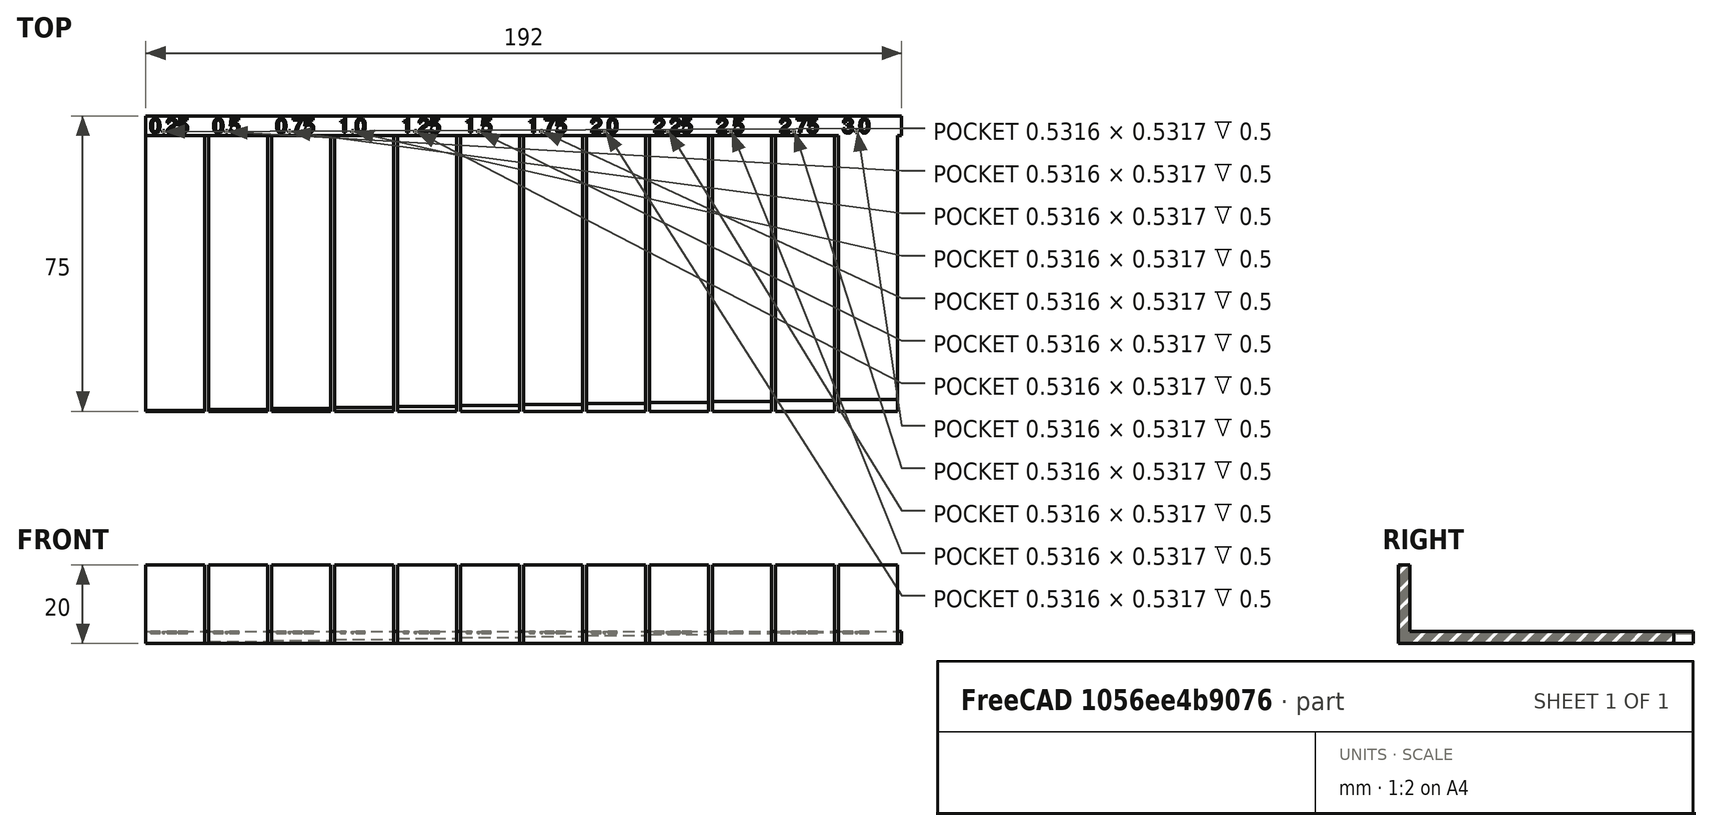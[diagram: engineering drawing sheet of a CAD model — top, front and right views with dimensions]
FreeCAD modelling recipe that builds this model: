
FCSTD DOCUMENT  (FreeCAD 0.18R16093 (Git))
Label: thickness test
License: All rights reserved
LicenseURL: http://en.wikipedia.org/wiki/All_rights_reserved
objects: Part::Box×25, Part::Part2DObjectPython×12, Part::Extrusion×12, Part::MultiFuse×4, App::DocumentObjectGroup×3, Part::Cut×1
note: 54 computed .brp shape members not serialized (recipe doc carries the construction recipe); baked Part::Feature solids carry a one-line shape summary decoded from their .brp

FEATURE [Part::Box] Box  label="Cube000"
  AttacherType = Attacher::AttachEngine3D
  Height = 0.25
  Length = 15
  Width = 70
FEATURE [Part::Box] Box001  label="Cube001"
  AttacherType = Attacher::AttachEngine3D
  Height = 0.5
  Length = 15
  Placement = pos=(16,0,0) rot=(0,0,1;0rad)
  Width = 70
FEATURE [Part::Box] Box002  label="Cube002"
  AttacherType = Attacher::AttachEngine3D
  Height = 0.75
  Length = 15
  Placement = pos=(32,0,0) rot=(0,0,1;0rad)
  Width = 70
FEATURE [Part::Box] Box003  label="Cube003"
  AttacherType = Attacher::AttachEngine3D
  Height = 1
  Length = 15
  Placement = pos=(48,0,0) rot=(0,0,1;0rad)
  Width = 70
FEATURE [Part::Box] Box004  label="Cube004"
  AttacherType = Attacher::AttachEngine3D
  Height = 1.25
  Length = 15
  Placement = pos=(64,0,0) rot=(0,0,1;0rad)
  Width = 70
FEATURE [Part::Box] Box005  label="Cube005"
  AttacherType = Attacher::AttachEngine3D
  Height = 1.5
  Length = 15
  Placement = pos=(80,0,0) rot=(0,0,1;0rad)
  Width = 70
FEATURE [Part::Box] Box006  label="Cube006"
  AttacherType = Attacher::AttachEngine3D
  Height = 1.75
  Length = 15
  Placement = pos=(96,0,0) rot=(0,0,1;0rad)
  Width = 70
FEATURE [Part::Box] Box007  label="Cube007"
  AttacherType = Attacher::AttachEngine3D
  Height = 2
  Length = 15
  Placement = pos=(112,0,0) rot=(0,0,1;0rad)
  Width = 70
FEATURE [Part::Box] Box008  label="Cube008"
  AttacherType = Attacher::AttachEngine3D
  Height = 2.25
  Length = 15
  Placement = pos=(128,0,0) rot=(0,0,1;0rad)
  Width = 70
FEATURE [Part::Box] Box009  label="Cube009"
  AttacherType = Attacher::AttachEngine3D
  Height = 2.5
  Length = 15
  Placement = pos=(144,0,0) rot=(0,0,1;0rad)
  Width = 70
FEATURE [Part::Box] Box010  label="Cube010"
  AttacherType = Attacher::AttachEngine3D
  Height = 2.75
  Length = 15
  Placement = pos=(160,0,0) rot=(0,0,1;0rad)
  Width = 70
FEATURE [Part::Box] Box011  label="Cube011"
  AttacherType = Attacher::AttachEngine3D
  Height = 3
  Length = 15
  Placement = pos=(176,0,0) rot=(0,0,1;0rad)
  Width = 70
FEATURE [Part::Box] Box012  label="Cube"
  AttacherType = Attacher::AttachEngine3D
  Height = 20
  Length = 15
  Width = 0.25
FEATURE [Part::Box] Box013  label="Cube012"
  AttacherType = Attacher::AttachEngine3D
  Height = 20
  Length = 15
  Placement = pos=(16,0,0) rot=(0,0,1;0rad)
  Width = 0.5
FEATURE [Part::Box] Box014  label="Cube013"
  AttacherType = Attacher::AttachEngine3D
  Height = 20
  Length = 15
  Placement = pos=(32,0,0) rot=(0,0,1;0rad)
  Width = 0.75
FEATURE [Part::Box] Box015  label="Cube014"
  AttacherType = Attacher::AttachEngine3D
  Height = 20
  Length = 15
  Placement = pos=(48,0,0) rot=(0,0,1;0rad)
  Width = 1
FEATURE [Part::Box] Box016  label="Cube015"
  AttacherType = Attacher::AttachEngine3D
  Height = 20
  Length = 15
  Placement = pos=(64,0,0) rot=(0,0,1;0rad)
  Width = 1.25
FEATURE [Part::Box] Box017  label="Cube016"
  AttacherType = Attacher::AttachEngine3D
  Height = 20
  Length = 15
  Placement = pos=(80,0,0) rot=(0,0,1;0rad)
  Width = 1.5
FEATURE [Part::Box] Box018  label="Cube017"
  AttacherType = Attacher::AttachEngine3D
  Height = 20
  Length = 15
  Placement = pos=(96,0,0) rot=(0,0,1;0rad)
  Width = 1.75
FEATURE [Part::Box] Box019  label="Cube018"
  AttacherType = Attacher::AttachEngine3D
  Height = 20
  Length = 15
  Placement = pos=(112,0,0) rot=(0,0,1;0rad)
  Width = 2
FEATURE [Part::Box] Box020  label="Cube019"
  AttacherType = Attacher::AttachEngine3D
  Height = 20
  Length = 15
  Placement = pos=(128,0,0) rot=(0,0,1;0rad)
  Width = 2.25
FEATURE [Part::Box] Box021  label="Cube020"
  AttacherType = Attacher::AttachEngine3D
  Height = 20
  Length = 15
  Placement = pos=(144,0,0) rot=(0,0,1;0rad)
  Width = 2.5
FEATURE [Part::Box] Box022  label="Cube021"
  AttacherType = Attacher::AttachEngine3D
  Height = 20
  Length = 15
  Placement = pos=(160,0,0) rot=(0,0,1;0rad)
  Width = 2.75
FEATURE [Part::Box] Box023  label="Cube022"
  AttacherType = Attacher::AttachEngine3D
  Height = 20
  Length = 15
  Placement = pos=(176,0,0) rot=(0,0,1;0rad)
  Width = 3
FEATURE [App::DocumentObjectGroup] Group001
FEATURE [Part::Box] Box024  label="Cube023"
  AttacherType = Attacher::AttachEngine3D
  Height = 3
  Length = 192
  Placement = pos=(0,70,0) rot=(0,0,1;0rad)
  Width = 5
FEATURE [Part::Part2DObjectPython] ShapeString001  # Draft 2D object (typed FeaturePython)
  FontFile = <path>
  Placement = pos=(17,70.75,3) rot=(0,0,1;0rad)
  Size = 2
  String = 0.5
  Tracking = 0
FEATURE [Part::Part2DObjectPython] ShapeString002  # Draft 2D object (typed FeaturePython)
  FontFile = <path>
  Placement = pos=(33,70.75,3) rot=(0,0,1;0rad)
  Size = 2
  String = 0.75
  Tracking = 0
FEATURE [Part::Part2DObjectPython] ShapeString003  # Draft 2D object (typed FeaturePython)
  FontFile = <path>
  Placement = pos=(49,70.75,3) rot=(0,0,1;0rad)
  Size = 2
  String = 1
  Tracking = 0
FEATURE [Part::Part2DObjectPython] ShapeString004  # Draft 2D object (typed FeaturePython)
  FontFile = <path>
  Placement = pos=(65,70.75,3) rot=(0,0,1;0rad)
  Size = 2
  String = 1.25
  Tracking = 0
FEATURE [Part::Part2DObjectPython] ShapeString005  # Draft 2D object (typed FeaturePython)
  FontFile = <path>
  Placement = pos=(81,70.75,3) rot=(0,0,1;0rad)
  Size = 2
  String = 1.5
  Tracking = 0
FEATURE [Part::Part2DObjectPython] ShapeString006  # Draft 2D object (typed FeaturePython)
  FontFile = <path>
  Placement = pos=(97,70.75,3) rot=(0,0,1;0rad)
  Size = 2
  String = 1.75
  Tracking = 0
FEATURE [Part::Part2DObjectPython] ShapeString007  # Draft 2D object (typed FeaturePython)
  FontFile = <path>
  Placement = pos=(113,70.75,3) rot=(0,0,1;0rad)
  Size = 2
  String = 2
  Tracking = 0
FEATURE [Part::Part2DObjectPython] ShapeString008  # Draft 2D object (typed FeaturePython)
  FontFile = <path>
  Placement = pos=(129,70.75,3) rot=(0,0,1;0rad)
  Size = 2
  String = 2.25
  Tracking = 0
  expr: Placement.Base.x = 113 + 16
FEATURE [Part::Part2DObjectPython] ShapeString009  # Draft 2D object (typed FeaturePython)
  FontFile = <path>
  Placement = pos=(145,70.75,3) rot=(0,0,1;0rad)
  Size = 2
  String = 2.5
  Tracking = 0
FEATURE [Part::Part2DObjectPython] ShapeString010  # Draft 2D object (typed FeaturePython)
  FontFile = <path>
  Placement = pos=(161,70.75,3) rot=(0,0,1;0rad)
  Size = 2
  String = 2.75
  Tracking = 0
FEATURE [Part::Part2DObjectPython] ShapeString011  # Draft 2D object (typed FeaturePython)
  FontFile = <path>
  Placement = pos=(177,70.75,3) rot=(0,0,1;0rad)
  Size = 2
  String = 3
  Tracking = 0
FEATURE [Part::Part2DObjectPython] ShapeString012  # Draft 2D object (typed FeaturePython)
  FontFile = <path>
  Placement = pos=(1,70.75,3) rot=(0,0,1;0rad)
  Size = 2
  String = 0.25
  Tracking = 0
FEATURE [App::DocumentObjectGroup] Group002
  Group = -> [ShapeString001,ShapeString002,ShapeString003,ShapeString004,ShapeString005,ShapeString006,ShapeString007,ShapeString008,ShapeString009,ShapeString010,ShapeString011,ShapeString012]
FEATURE [Part::Extrusion] Extrude
  Base = -> ShapeString001
  Dir = (0,0,1)
  DirMode = 2
  FaceMakerClass = Part::FaceMakerBullseye
  LengthFwd = 0
  LengthRev = 0.5
  Solid = false
  Symmetric = false
FEATURE [Part::Extrusion] Extrude001
  Base = -> ShapeString002
  Dir = (0,0,1)
  DirMode = 2
  FaceMakerClass = Part::FaceMakerBullseye
  LengthFwd = 0
  LengthRev = 0.5
  Solid = false
  Symmetric = false
FEATURE [Part::Extrusion] Extrude002
  Base = -> ShapeString003
  Dir = (0,0,1)
  DirMode = 2
  FaceMakerClass = Part::FaceMakerBullseye
  LengthFwd = 0
  LengthRev = 0.5
  Solid = false
  Symmetric = false
FEATURE [Part::Extrusion] Extrude003
  Base = -> ShapeString004
  Dir = (0,0,1)
  DirMode = 2
  FaceMakerClass = Part::FaceMakerBullseye
  LengthFwd = 0
  LengthRev = 0.5
  Solid = false
  Symmetric = false
FEATURE [Part::Extrusion] Extrude004
  Base = -> ShapeString005
  Dir = (0,0,1)
  DirMode = 2
  FaceMakerClass = Part::FaceMakerBullseye
  LengthFwd = 0
  LengthRev = 0.5
  Solid = false
  Symmetric = false
FEATURE [Part::Extrusion] Extrude005
  Base = -> ShapeString006
  Dir = (0,0,1)
  DirMode = 2
  FaceMakerClass = Part::FaceMakerBullseye
  LengthFwd = 0
  LengthRev = 0.5
  Solid = false
  Symmetric = false
FEATURE [Part::Extrusion] Extrude006
  Base = -> ShapeString007
  Dir = (0,0,1)
  DirMode = 2
  FaceMakerClass = Part::FaceMakerBullseye
  LengthFwd = 0
  LengthRev = 0.5
  Solid = false
  Symmetric = false
FEATURE [Part::Extrusion] Extrude007
  Base = -> ShapeString008
  Dir = (0,0,1)
  DirMode = 2
  FaceMakerClass = Part::FaceMakerBullseye
  LengthFwd = 0
  LengthRev = 0.5
  Solid = false
  Symmetric = false
FEATURE [Part::Extrusion] Extrude008
  Base = -> ShapeString009
  Dir = (0,0,1)
  DirMode = 2
  FaceMakerClass = Part::FaceMakerBullseye
  LengthFwd = 0
  LengthRev = 0.5
  Solid = false
  Symmetric = false
FEATURE [Part::Extrusion] Extrude009
  Base = -> ShapeString010
  Dir = (0,0,1)
  DirMode = 2
  FaceMakerClass = Part::FaceMakerBullseye
  LengthFwd = 0
  LengthRev = 0.5
  Solid = false
  Symmetric = false
FEATURE [Part::Extrusion] Extrude010
  Base = -> ShapeString011
  Dir = (0,0,1)
  DirMode = 2
  FaceMakerClass = Part::FaceMakerBullseye
  LengthFwd = 0
  LengthRev = 0.5
  Solid = false
  Symmetric = false
FEATURE [Part::Extrusion] Extrude011
  Base = -> ShapeString012
  Dir = (0,0,1)
  DirMode = 2
  FaceMakerClass = Part::FaceMakerBullseye
  LengthFwd = 0
  LengthRev = 0.5
  Solid = false
  Symmetric = false
FEATURE [Part::MultiFuse] Fusion
  Shapes = -> [Extrude,Extrude001,Extrude002,Extrude003,Extrude004,Extrude005,Extrude006,Extrude007,Extrude008,Extrude009,Extrude010,Extrude011]
FEATURE [Part::Cut] Cut
  Base = -> Box024
  Tool = -> Fusion
FEATURE [Part::MultiFuse] Fusion001
  Shapes = -> [Box,Box010,Box002,Box003,Box005,Box001,Box006,Box007,Box009,Box008,Box004,Box011]
FEATURE [Part::MultiFuse] Fusion002
  Shapes = -> [Box012,Box016,Box020,Box015,Box017,Box018,Box023,Box022,Box021,Box014,Box019,Box013]
FEATURE [Part::MultiFuse] Fusion003
  Shapes = -> [Cut,Fusion002,Fusion001]
FEATURE [App::DocumentObjectGroup] Group
  Group = -> [Fusion003]
note: 12 file-system paths scrubbed to <path> (originals preserved in the JSON sidecar)
